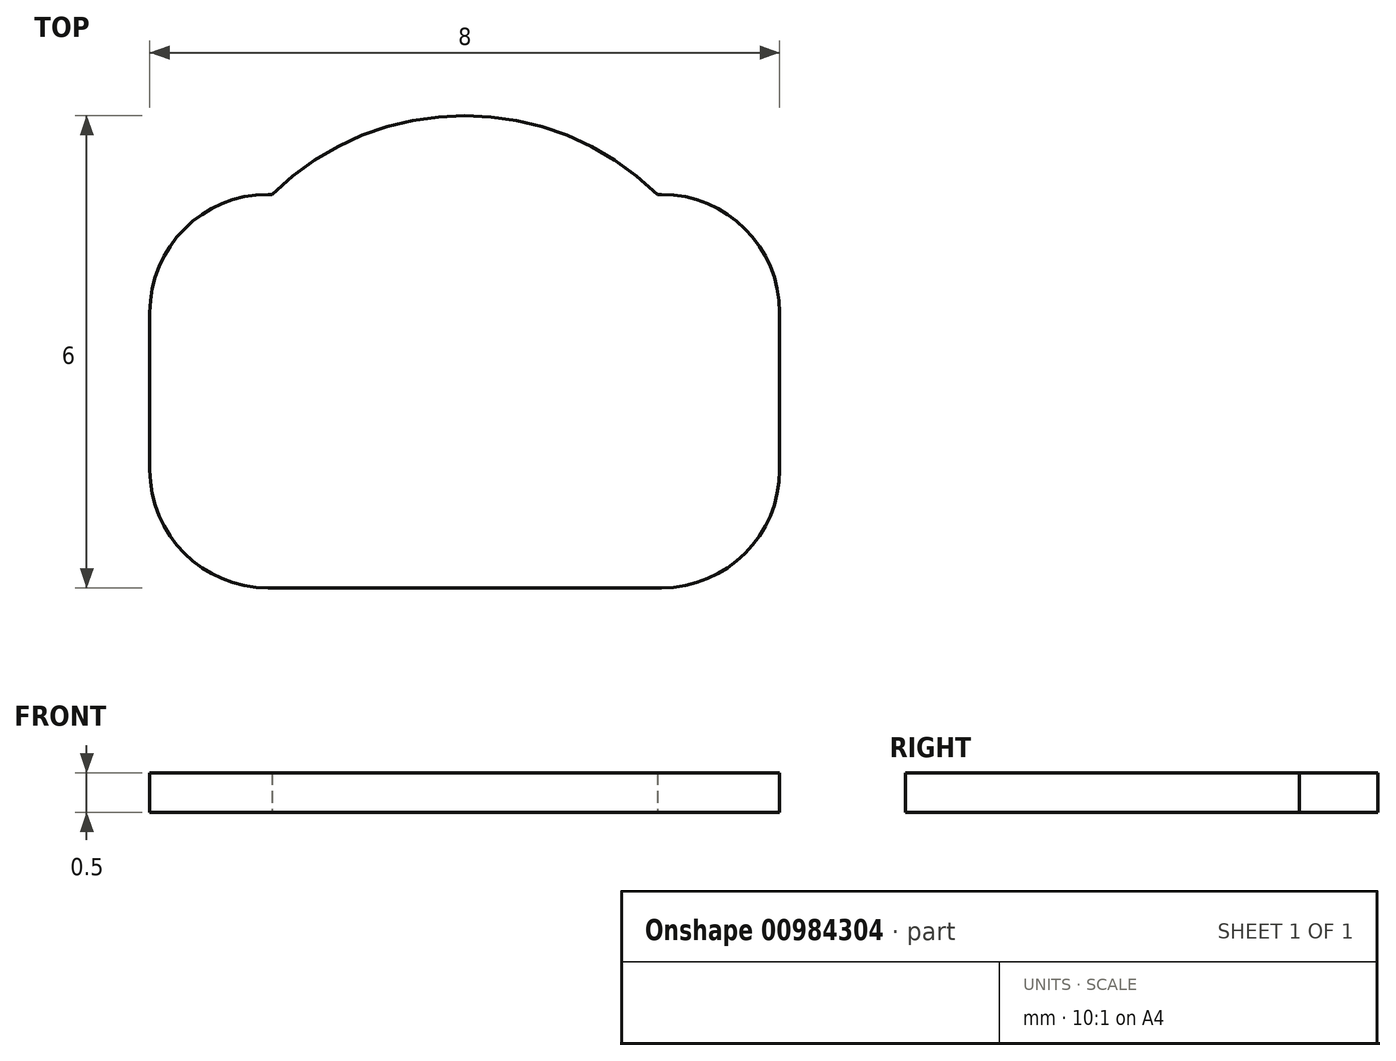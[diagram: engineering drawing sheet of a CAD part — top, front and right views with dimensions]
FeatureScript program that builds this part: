
annotation { "Feature Type Name" : "Feature", "Feature Type Description" : "" }
export const myFeature = defineFeature(function(context is Context, id is Id, definition is map)
    precondition{}
    {
        {
            var Q0;
            Q0=qCreatedBy(makeId("Top.planeOp"),FACE);
            var sketch = newSketch(context, id + "F0", { "sketchPlane" : qUnion([Q0])});
            skCircle(sketch, "E0", {"center": v(0, 0) * mm, "radius": 3.5 * mm});
            skLineSegment(sketch, "E1.bottom", {"start": v(4, -2.5) * mm, "end": v(-4, -2.5) * mm});
            skLineSegment(sketch, "E1.top", {"start": v(4, 2.5) * mm, "end": v(-4, 2.5) * mm});
            skLineSegment(sketch, "E1.left", {"start": v(4, -2.5) * mm, "end": v(4, 2.5) * mm});
            skLineSegment(sketch, "E1.right", {"start": v(-4, -2.5) * mm, "end": v(-4, 2.5) * mm});
            skSolve(sketch);
        }
        {
            var Q0;
            {var subQ0=sQuery(id+"F0.wireOp",EDGE,"E1.top");var subQ1=sQuery(id+"F0.wireOp",EDGE,"E0");var subQ2=makeQuery(id+"F0.imprint","INTERSECT",VERTEX,{"disambiguationData":[OD(0.0)],"derivedFrom":[subQ1,subQ0]});Q0=makeQuery(id+"F0.imprint","IMPRINT",FACE,{"disambiguationData":[TD([[makeQuery(id+"F0.imprint","IMPRINT",EDGE,{"disambiguationData":[TD([[subQ2,-1.0]])],"derivedFrom":subQ1}),1.0]])]});}
            var Q1;
            {var subQ0=sQuery(id+"F0.wireOp",EDGE,"E1.top");var subQ1=sQuery(id+"F0.wireOp",EDGE,"E0");var subQ2=makeQuery(id+"F0.imprint","INTERSECT",VERTEX,{"disambiguationData":[OD(0.0)],"derivedFrom":[subQ1,subQ0]});Q1=makeQuery(id+"F0.imprint","IMPRINT",FACE,{"disambiguationData":[TD([[makeQuery(id+"F0.imprint","IMPRINT",EDGE,{"disambiguationData":[TD([[subQ2,1.0]])],"derivedFrom":subQ1}),1.0]])]});}
            var Q2;
            {var subQ5=sQuery(id+"F0.wireOp",EDGE,"E1.left");Q2=makeQuery(id+"F0.imprint","IMPRINT",FACE,{"disambiguationData":[TD([[makeQuery(id+"F0.imprint","IMPRINT",EDGE,{"derivedFrom":subQ5}),1.0]])]});}
            var Q3;
            {var subQ0=sQuery(id+"F0.wireOp",EDGE,"E1.bottom");var subQ1=sQuery(id+"F0.wireOp",EDGE,"E0");var subQ2=makeQuery(id+"F0.imprint","INTERSECT",VERTEX,{"disambiguationData":[OD(0.0)],"derivedFrom":[subQ1,subQ0]});Q3=makeQuery(id+"F0.imprint","IMPRINT",FACE,{"disambiguationData":[TD([[makeQuery(id+"F0.imprint","IMPRINT",EDGE,{"disambiguationData":[TD([[subQ2,-1.0]])],"derivedFrom":subQ1}),1.0]])]});}
            var Q4;
            {var subQ5=sQuery(id+"F0.wireOp",EDGE,"E1.right");Q4=makeQuery(id+"F0.imprint","IMPRINT",FACE,{"disambiguationData":[TD([[makeQuery(id+"F0.imprint","IMPRINT",EDGE,{"derivedFrom":subQ5}),-1.0]])]});}
            extrude(context, id + "F1", {"entities" : qUnion([Q0, Q1, Q2, Q3, Q4]), "depth" : 0.5 * mm, "offsetDistance" : 25 * mm});
        }
        {
            var Q0;
            Q0=makeQuery(id+"F1.opExtrude","SWEPT_EDGE",EDGE,{"disambiguationData":[OSD([sQuery(id+"F0.wireOp",EDGE,"E1.bottom"),sQuery(id+"F0.wireOp",EDGE,"E1.right")])]});
            var Q1;
            Q1=makeQuery(id+"F1.opExtrude","SWEPT_EDGE",EDGE,{"disambiguationData":[OSD([sQuery(id+"F0.wireOp",EDGE,"E1.top"),sQuery(id+"F0.wireOp",EDGE,"E1.right")])]});
            var Q2;
            Q2=makeQuery(id+"F1.opExtrude","SWEPT_EDGE",EDGE,{"disambiguationData":[OSD([sQuery(id+"F0.wireOp",EDGE,"E1.bottom"),sQuery(id+"F0.wireOp",EDGE,"E1.left")])]});
            var Q3;
            Q3=makeQuery(id+"F1.opExtrude","SWEPT_EDGE",EDGE,{"disambiguationData":[OSD([sQuery(id+"F0.wireOp",EDGE,"E1.top"),sQuery(id+"F0.wireOp",EDGE,"E1.left")])]});
            fillet(context, id + "F2", {"entities" : qUnion([Q0, Q1, Q2, Q3]), "radius" : 1.5 * mm, "tangentPropagation" : true, "allowEdgeOverflow" : false});
        }
    });
